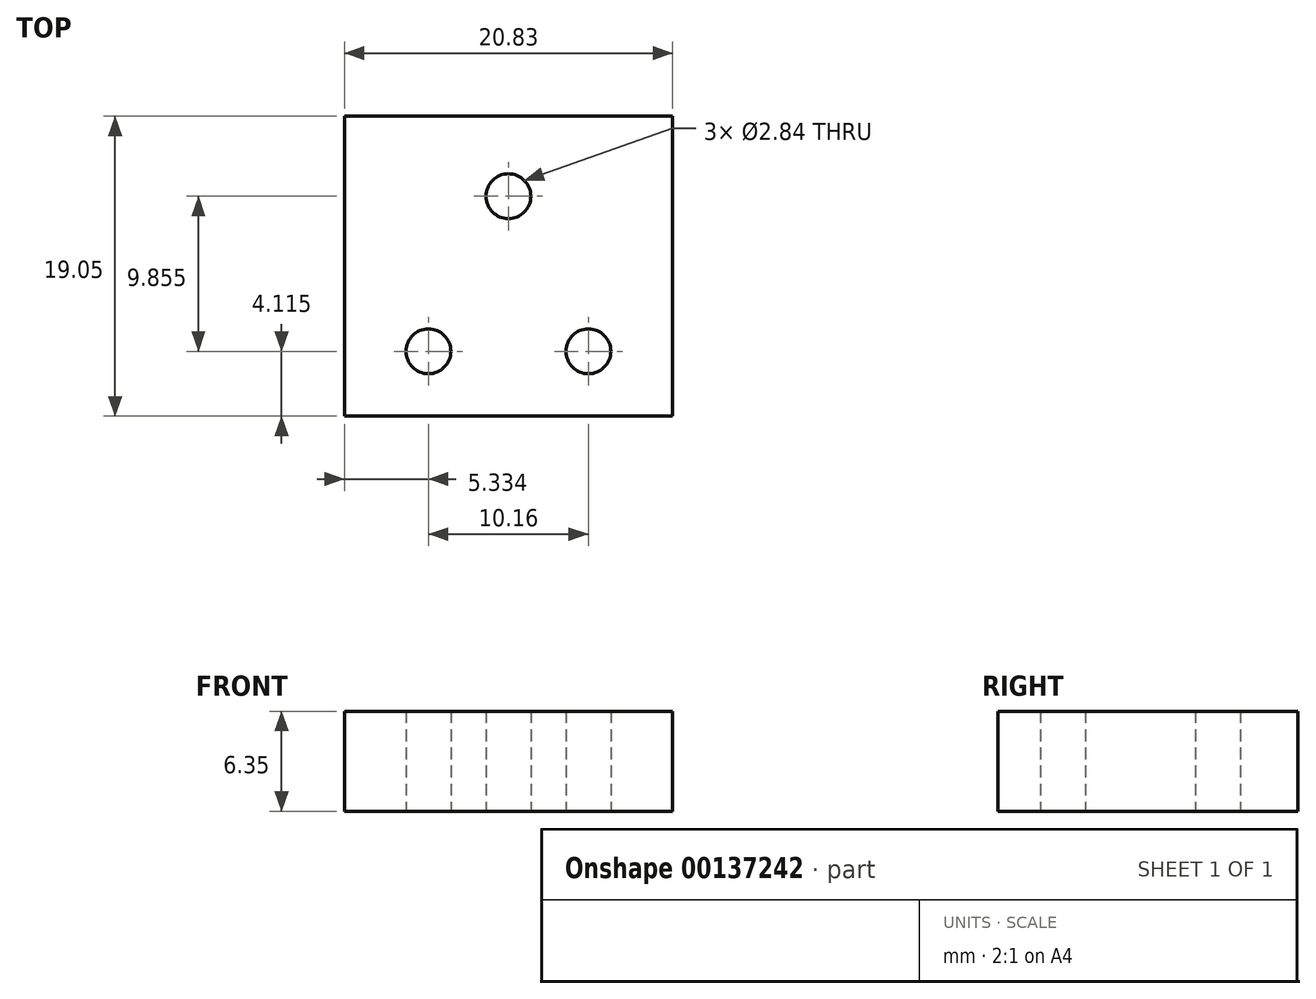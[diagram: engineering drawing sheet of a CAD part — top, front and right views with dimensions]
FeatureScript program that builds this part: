
annotation { "Feature Type Name" : "Feature", "Feature Type Description" : "" }
export const myFeature = defineFeature(function(context is Context, id is Id, definition is map)
    precondition{}
    {
        {
            var Q0;
            Q0=qCreatedBy(makeId("Top.planeOp"),FACE);
            var sketch = newSketch(context, id + "F0", { "sketchPlane" : qUnion([Q0])});
            skLineSegment(sketch, "E0.bottom", {"start": v(0, 0) * mm, "end": v(20.83, 0) * mm});
            skLineSegment(sketch, "E0.top", {"start": v(0, 19.05) * mm, "end": v(20.83, 19.05) * mm});
            skLineSegment(sketch, "E0.left", {"start": v(0, 0) * mm, "end": v(0, 19.05) * mm});
            skLineSegment(sketch, "E0.right", {"start": v(20.83, 0) * mm, "end": v(20.83, 19.05) * mm});
            skCircle(sketch, "E1", {"center": v(10.41, 13.97) * mm, "radius": 1.42 * mm});
            skCircle(sketch, "E2", {"center": v(5.33, 4.11) * mm, "radius": 1.42 * mm});
            skCircle(sketch, "E3", {"center": v(15.5, 4.11) * mm, "radius": 1.42 * mm});
            skSolve(sketch);
        }
        {
            var Q0;
            Q0=makeQuery(id+"F0.imprint","IMPRINT",FACE,{"disambiguationData":[TD([[makeQuery(id+"F0.imprint","IMPRINT",EDGE,{"derivedFrom":sQuery(id+"F0.wireOp",EDGE,"E0.bottom")}),1.0]])]});
            extrude(context, id + "F1", {"entities" : qUnion([Q0]), "depth" : 6.35 * mm});
        }
    });
